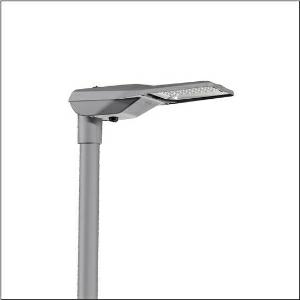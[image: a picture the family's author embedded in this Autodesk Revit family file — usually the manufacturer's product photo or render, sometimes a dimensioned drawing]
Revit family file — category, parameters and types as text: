
# Revit family: streetlight_sl_21_mini___p0_8ab_5xe2r33t08jb_257d
name_source: partatom
category: Lighting Fixtures
units: mm (PartAtom-declared; Revit-internal decimal feet)

## family parameters
Cut with Voids When Loaded = No
Host = Face
Light Source = No
Part Type = Normal
Room Calculation Point = No
Round Connector Dimension = Use Diameter
Shared = No

## types (1)
- --- (1 x LED, 11230 lm, 88.6 W, 3000K)
    Apparent Load = 89 VA
    CIE Flux Codes = 39 72 97 100 100
    Color Rendering = 70
    Color Temperature = 3000K
    Default Elevation = 1800 mm
    Description = Streetlight SL 21 mini, mast luminaire, primary light control with lens, of PMMA, primary optical cover: cover, of toughened safety glass, transparent, light distribution: P0.8aB, light emission: direct distribution, primary light characteristic: asymmetric, installation type: post-top, side-entry, LED, High Power LED, rated luminous flux: 11.230lm, luminous efficacy: 127lm/W, light colour: 730, colour temperature: 3000K, control gear: D4i, control: pre-setting: logarithmic dimming characteristic, flexible luminous flux parameterisation, time-dependent luminous flux control, constant luminous flux control, overheat protection, mains connection: 220..240V, AC, 50/60Hz, start of lifetime: 89W, end of service life: 92W, reduction: 41W, luminaire housing, of diecast aluminium, powder-coated, Siteco® metallic grey (DB 702S), corrosivity category C5 mid according to DIN EN ISO 12944, multi-level sealing system, sealing non-destructively replaceable, inclination adjustable: 0°, 5°, 10°, 15°, please order mast flange separately, length: 628mm, width: 235mm, height: 110mm, mast flange for spigot size: 42mm (side-entry): 5XC10008XM4, 60/48mm (side-entry/post-top): 5XC10108XM2, 76/60mm (side-entry/post-top): 5XC10108XM1, mounting height: 4..8m, Smart Interface below and above, protection rating (complete): IP66, insulation class (complete): insulation class II (safety insulation), certification: CE, ENEC, ENEC+, VDE, impact resistance: IK10, permissible operating ambient temperature for outdoor applications: -40..+50°C, standard-compliant lighting for roads and squares, packaging unit: 1 piece

Light Distribution: P0.8aB
    Height = 110 mm
    Lamp = 1 x LED
    Lamp Light Flux = 11230 lm
    Lamp Power = 88.6 W
    Lamp count = 1
    Length = 625 mm
    Luminous efficacy = 127 lm/W
    Manufacturer = Siteco
    ModVariant = No
    Model = 5XE2R33T08JB
    Number of Poles = 1
    OnlyDefault = Yes
    Power Factor = 1
    Product Name = Streetlight SL 21 mini | P0.8aB
    Product group = mast luminaire | pylon top
    ProductGroupID = 6100
    Protection Class = Protection class II
    Protection Degree = IP 66
    RLX_Detail_Level = 1
    RLX_Emergency_Light_Flux = 0 lm
    RLX_Emergency_Type = 0
    RLX_Emergency_Type_DB = No
    RlxData = <blob elided: 26053 chars, md5=2a29fc80>
    Socket = socket
    Standby Power = 0 W
    System Light Flux = 11230 lm
    System Power = 89 W
    Type Comments = factory setting: luminous flux: 100 % | dim-lin: 254 | 915 mA
    Type Image = l_1003514.jpg
    URL = http://relux.com
    VarID = @adj_033167
    Voltage = 0 V
    Weight = 0.00 kg
    Width = 234 mm

## geometry (parser evidence)
native form markers: Blend x4, Sweep x12
no freeform markers — native parametric forms only
